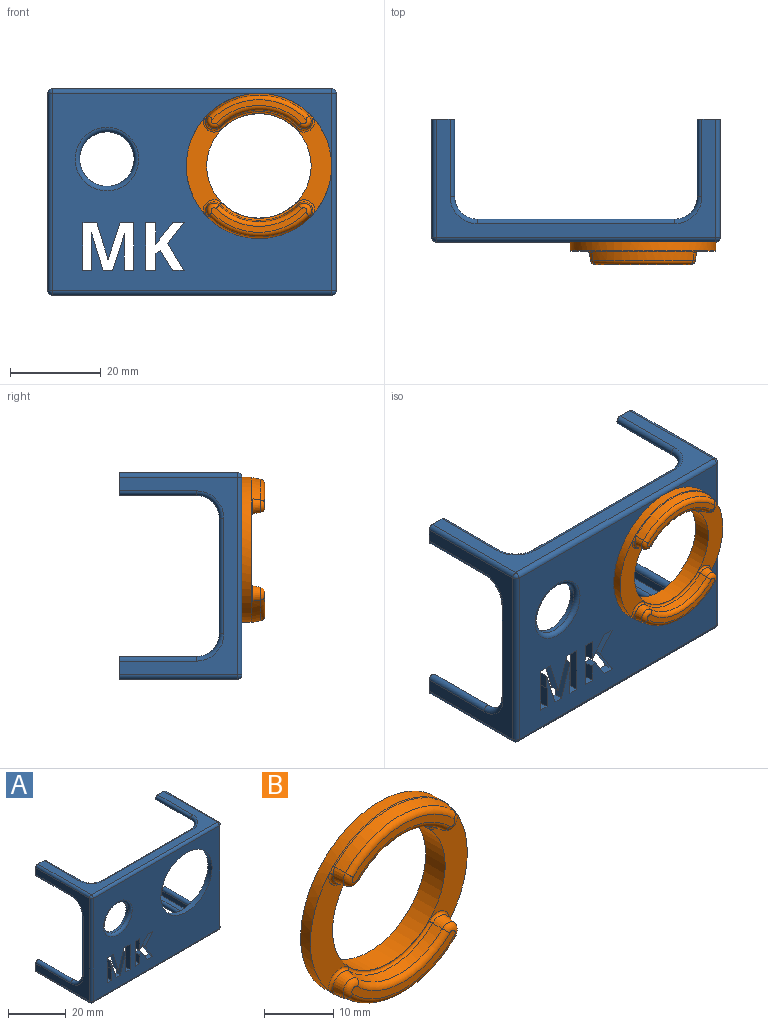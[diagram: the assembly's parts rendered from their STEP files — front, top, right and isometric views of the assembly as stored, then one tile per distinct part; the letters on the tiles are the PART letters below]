
ASSEMBLY  parts=2 mates=1
PART A: 81 faces, bbox 63.5x27x45.5 mm
  f0: plane 61.5x43.5mm, normal (0,-1,0), area 1904mm2, adj f15,f19,f20,f24,f25,f28,f29,f30
  f1: plane 59.5x41.5mm, normal (0,1,0), area 1738.8mm2, adj f5,f6,f12,f13,f14,f15,f29,f30
  f2: plane 5x5mm, normal (0,1,0), area 14.9mm2, adj f4,f5,f7,f13,f18,f65,f76
  f3: plane 5x5mm, normal (0,1,0), area 14.9mm2, adj f6,f7,f11,f13,f16,f70,f80
  f4: plane 61.5x26mm, normal (0,0,1), area 338mm2, adj f2,f8,f18,f24,f27,f61,f62,f63
  f5: plane 59.5x25mm, normal (0,0,-1), area 226.5mm2, adj f1,f2,f8,f12,f13,f61,f62,f63
  f6: plane 59.5x25mm, normal (0,0,1), area 226.5mm2, adj f1,f3,f10,f12,f13,f66,f67,f68
  f7: plane 43.5x26mm, normal (1,0,0), area 284mm2, adj f2,f3,f16,f18,f19,f76,f77,f78
  f8: plane 5x5mm, normal (0,1,0), area 14.9mm2, adj f4,f5,f9,f12,f27,f61,f71
  f9: plane 43.5x26mm, normal (-1,0,0), area 284mm2, adj f8,f10,f21,f25,f27,f71,f72,f73
  f10: plane 5x5mm, normal (0,1,0), area 14.9mm2, adj f6,f9,f11,f12,f21,f66,f75
  f11: plane 61.5x26mm, normal (0,0,-1), area 338mm2, adj f3,f10,f16,f20,f21,f66,f67,f68
  f12: plane 41.5x25mm, normal (1,0,0), area 190.5mm2, adj f1,f5,f6,f8,f10,f71,f72,f73
  f13: plane 41.5x25mm, normal (-1,0,0), area 190.5mm2, adj f1,f2,f3,f5,f6,f76,f77,f78
  f14: cylinder r=6mm len=12mm, axis (0,1,0), area 37.7mm2, adj f1,f28
  f15: cylinder r=12.5mm len=25mm, axis (0,1,0), area 157.1mm2, adj f0,f1
  f16: cylinder r=1mm len=26mm, axis (0,-1,0), area 40.8mm2, adj f3,f7,f11,f17
  f17: sphere r=1mm, area 1.6mm2, adj f16,f19,f20
  f18: cylinder r=1mm len=26mm, axis (0,1,0), area 40.8mm2, adj f2,f4,f7,f22
  f19: cylinder r=1mm len=43.5mm, axis (0,0,-1), area 68.3mm2, adj f0,f7,f17,f22
  f20: cylinder r=1mm len=61.5mm, axis (-1,0,0), area 96.6mm2, adj f0,f11,f17,f23
  f21: cylinder r=1mm len=26mm, axis (0,1,0), area 40.8mm2, adj f9,f10,f11,f23
  f22: sphere r=1mm, area 1.6mm2, adj f18,f19,f24
  f23: sphere r=1mm, area 1.6mm2, adj f20,f21,f25
  f24: cylinder r=1mm len=61.5mm, axis (1,0,0), area 96.6mm2, adj f0,f4,f22,f26
  f25: cylinder r=1mm len=43.5mm, axis (0,0,1), area 68.3mm2, adj f0,f9,f23,f26
  f26: sphere r=1mm, area 1.6mm2, adj f24,f25,f27
  f27: cylinder r=1mm len=26mm, axis (0,-1,0), area 40.8mm2, adj f4,f8,f9,f26
  f28: torus R=7mm, axis (0,-1,0), area 62.8mm2, adj f0,f14
  f29: plane 5.85x3.69mm, normal (-0.85,0,-0.53), area 13.8mm2, adj f0,f1,f30,f41
  f30: plane 4.64x3.66mm, normal (-0.79,0,0.62), area 11.8mm2, adj f0,f1,f29,f31
  f31: plane 2.47x2mm, normal (0,0,-1), area 4.9mm2, adj f0,f1,f30,f32
  f32: plane 3.57x2.84mm, normal (0.78,0,-0.62), area 9.1mm2, adj f0,f1,f31,f33
  f33: plane 2x1.24mm, normal (0.82,0,-0.58), area 3mm2, adj f0,f1,f32,f34
  f34: plane 4.8x2mm, normal (-1,0,0), area 9.6mm2, adj f0,f1,f33,f35
  f35: plane 2.23x2mm, normal (0,0,-1), area 4.5mm2, adj f0,f1,f34,f36
  f36: plane 10.49x2mm, normal (1,0,0), area 21mm2, adj f0,f1,f35,f37
  f37: plane 2.23x2mm, normal (0,0,1), area 4.5mm2, adj f0,f1,f36,f38
  f38: plane 3.75x2mm, normal (-1,0,0), area 7.5mm2, adj f0,f1,f37,f39
  f39: plane 2x0.94mm, normal (-0.58,0,0.81), area 2.3mm2, adj f0,f1,f38,f40
  f40: plane 4.42x2.75mm, normal (0.85,0,0.53), area 10.4mm2, adj f0,f1,f39,f41
  f41: plane 2.53x2mm, normal (0,0,1), area 5.1mm2, adj f0,f1,f29,f40
  f42: plane 2.04x2mm, normal (0,0,1), area 4.1mm2, adj f0,f1,f43,f60
  f43: plane 8.22x2.71mm, normal (-0.95,0,0.31), area 17.3mm2, adj f0,f1,f42,f44
  f44: plane 2x0.06mm, normal (0,0,1), area 0.1mm2, adj f0,f1,f43,f45
  f45: extruded ~2.44x2mm, area 4.9mm2, adj f0,f1,f44,f46
  f46: extruded ~2x0.81mm, area 1.6mm2, adj f0,f1,f45,f47
  f47: plane 4.97x2mm, normal (1,0,0), area 9.9mm2, adj f0,f1,f46,f48
  f48: plane 2.07x2mm, normal (0,0,1), area 4.1mm2, adj f0,f1,f47,f49
  f49: plane 10.49x2mm, normal (-1,0,0), area 21mm2, adj f0,f1,f48,f50
  f50: plane 3.03x2mm, normal (0,0,-1), area 6.1mm2, adj f0,f1,f49,f51
  f51: plane 8.03x2.63mm, normal (0.95,0,-0.31), area 16.9mm2, adj f0,f1,f50,f52
  f52: plane 2x0.04mm, normal (0,0,-1), area 0.1mm2, adj f0,f1,f51,f53
  f53: plane 8.03x2.48mm, normal (-0.96,0,-0.3), area 16.8mm2, adj f0,f1,f52,f54
  f54: plane 3.03x2mm, normal (0,0,-1), area 6.1mm2, adj f0,f1,f53,f55
  f55: plane 10.49x2mm, normal (1,0,0), area 21mm2, adj f0,f1,f54,f56
  f56: plane 2x1.99mm, normal (0,0,1), area 4mm2, adj f0,f1,f55,f57
  f57: plane 4.88x2mm, normal (-1,0,0), area 9.8mm2, adj f0,f1,f56,f58
  f58: extruded ~3.35x2mm, area 6.7mm2, adj f0,f1,f57,f59
  f59: plane 2x0.06mm, normal (0,0,1), area 0.1mm2, adj f0,f1,f58,f60
  f60: plane 8.23x2.53mm, normal (0.96,0,0.29), area 17.2mm2, adj f0,f1,f42,f59
  f61: cylinder r=1mm len=17mm, axis (0,-1,0), area 53.4mm2, adj f4,f5,f8,f62
  f62: torus R=6mm, axis (0,0,1), area 26.5mm2, adj f4,f5,f61,f63
  f63: cylinder r=1mm len=43.5mm, axis (1,0,0), area 136.7mm2, adj f4,f5,f62,f64
  f64: torus R=6mm, axis (0,0,1), area 26.5mm2, adj f4,f5,f63,f65
  f65: cylinder r=1mm len=17mm, axis (0,1,0), area 53.4mm2, adj f2,f4,f5,f64
  f66: cylinder r=1mm len=17mm, axis (0,1,0), area 53.4mm2, adj f6,f10,f11,f67
  f67: torus R=6mm, axis (0,0,1), area 26.5mm2, adj f6,f11,f66,f68
  f68: cylinder r=1mm len=43.5mm, axis (-1,0,0), area 136.7mm2, adj f6,f11,f67,f69
  f69: torus R=6mm, axis (0,0,1), area 26.5mm2, adj f6,f11,f68,f70
  f70: cylinder r=1mm len=17mm, axis (0,-1,0), area 53.4mm2, adj f3,f6,f11,f69
  f71: cylinder r=1mm len=17mm, axis (0,1,0), area 53.4mm2, adj f8,f9,f12,f72
  f72: torus R=6mm, axis (1,0,0), area 26.5mm2, adj f9,f12,f71,f73
  f73: cylinder r=1mm len=25.5mm, axis (0,0,1), area 80.1mm2, adj f9,f12,f72,f74
  f74: torus R=6mm, axis (1,0,0), area 26.5mm2, adj f9,f12,f73,f75
  f75: cylinder r=1mm len=17mm, axis (0,-1,0), area 53.4mm2, adj f9,f10,f12,f74
  f76: cylinder r=1mm len=17mm, axis (0,1,0), area 53.4mm2, adj f2,f7,f13,f77
  f77: torus R=6mm, axis (1,0,0), area 26.5mm2, adj f7,f13,f76,f78
  f78: cylinder r=1mm len=25.5mm, axis (0,0,1), area 80.1mm2, adj f7,f13,f77,f79
  f79: torus R=6mm, axis (1,0,0), area 26.5mm2, adj f7,f13,f78,f80
  f80: cylinder r=1mm len=17mm, axis (0,-1,0), area 53.4mm2, adj f3,f7,f13,f79
PART B: 33 faces, bbox 32x7x33.8 mm
  f0: plane 32.02x23.11mm, normal (0,-1,0), area 160.7mm2, adj f2,f4,f24,f26,f28,f30,f31,f32
  f1: cylinder r=12.45mm len=24.9mm, axis (0,1,0), area 156.5mm2, adj f3,f5
  f2: cylinder r=11.5mm len=23mm, axis (0,1,0), area 289mm2, adj f0,f3
  f3: plane 24.9x24.9mm, normal (0,1,0), area 71.5mm2, adj f1,f2
  f4: cylinder r=16mm len=32mm, axis (0,1,0), area 201.1mm2, adj f0,f5,f13,f25,f27,f29
  f5: plane 32x32mm, normal (0,1,0), area 317.3mm2, adj f1,f4
  f6: cone r=1.99mm half-angle=10deg, axis (0,1,0), area 10mm2, adj f7,f9,f17,f28,f29
  f7: cone r=11.96mm half-angle=10deg, axis (0,-1,0), area 34.2mm2, adj f6,f8,f16,f26
  f8: cone r=1.99mm half-angle=10deg, axis (0,1,0), area 10mm2, adj f7,f9,f18,f24,f25
  f9: cone r=15.95mm half-angle=10deg, axis (0,1,0), area 49.5mm2, adj f6,f8,f19,f27
  f10: plane 20.99x5.34mm, normal (0,-1,0), area 28.7mm2, adj f16,f17,f18,f19
  f11: cone r=11.96mm half-angle=10deg, axis (0,-1,0), area 34.2mm2, adj f12,f14,f23,f31
  f12: cone r=2.02mm half-angle=10deg, axis (0,1,0), area 10.1mm2, adj f11,f13,f21,f32
  f13: cone r=16mm half-angle=10deg, axis (0,1,0), area 55.4mm2, adj f4,f12,f14,f20,f30,f32
  f14: cone r=2.02mm half-angle=10deg, axis (0,1,0), area 10.1mm2, adj f11,f13,f22,f30
  f15: plane 21.07x5.4mm, normal (0,-1,0), area 29.9mm2, adj f20,f21,f22,f23
  f16: torus R=13.33mm, axis (0,-1,0), area 27.9mm2, adj f7,f10,f17,f18
  f17: torus R=0.63mm, axis (0,-1,0), area 5.3mm2, adj f6,f10,f16,f19
  f18: torus R=0.63mm, axis (0,-1,0), area 5.3mm2, adj f8,f10,f16,f19
  f19: torus R=14.58mm, axis (0,-1,0), area 33.3mm2, adj f9,f10,f17,f18
  f20: torus R=14.63mm, axis (0,-1,0), area 33.4mm2, adj f13,f15,f21,f22
  f21: torus R=0.65mm, axis (0,-1,0), area 5.4mm2, adj f12,f15,f20,f23
  f22: torus R=0.65mm, axis (0,-1,0), area 5.4mm2, adj f14,f15,f20,f23
  f23: torus R=13.33mm, axis (0,-1,0), area 27.9mm2, adj f11,f15,f21,f22
  f24: bspline ~4.12x4.12mm, area 3.8mm2, adj f0,f8,f25,f26
  f25: bspline ~1.1x0.99mm, area 0.5mm2, adj f4,f8,f24,f27
  f26: bspline ~17.02x3.87mm, area 13.2mm2, adj f0,f7,f24,f28
  f27: bspline ~22.63x4.75mm, area 5.5mm2, adj f4,f9,f25,f29
  f28: bspline ~4.12x4.12mm, area 3.8mm2, adj f0,f6,f26,f29
  f29: bspline ~1.1x0.99mm, area 0.5mm2, adj f4,f6,f27,f28
  f30: bspline ~4.16x4.16mm, area 4.3mm2, adj f0,f13,f14,f31
  f31: bspline ~17.02x3.87mm, area 13.2mm2, adj f0,f11,f30,f32
  f32: bspline ~4.16x4.16mm, area 4.3mm2, adj f0,f12,f13,f31
PLACE A at identity
PLACE B t=(17.98,-25,6.68)mm
MATE cylindrical B.f1 <-> A.f15  axis (0,1,0) through (17.98,-27,6.68)mm
